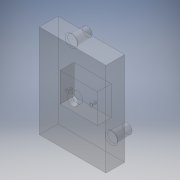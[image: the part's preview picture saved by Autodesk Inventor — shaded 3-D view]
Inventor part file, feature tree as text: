
AUTODESK INVENTOR PART (.ipt)
format: ipt  version: 2019 (Build 230136000, 136)  size: 160,768 bytes
history: native  units: mm
features: reference x14, other x5, extrude x4, sketch x4, fillet x3
ambient origin geometry x8: Origin, YZ Plane, XZ Plane, XY Plane, X Axis, Y Axis, Z Axis, Center Point
bodies: Solid1 (feature_tree)
feature tree (30):
  extrude  "Extrusion1"  Depth=7.0mm TaperAngle=0.0deg
  extrude  "Extrusion3"  Depth=6.0mm
  extrude  "Extrusion4"  Depth=5.2mm
  extrude  "Extrusion5"  Depth=0.2mm
  fillet  "Fillet1"  Radius=0.4mm
  fillet  "Fillet2"  Radius=0.5mm
  fillet  "Fillet3"  Radius=1.0mm
  sketch  "Sketch1"  dims[d0=4.0mm d1=7.0mm d2=0.0mm]
  reference  "Reference1"
  reference  "Reference2"
  reference  "Reference3"
  reference  "Reference4"
  sketch  "Sketch2"  dims[d9=3.8mm d10=6.0mm d11=-0.174533mm]
  reference  "Reference5"
  reference  "Reference6"
  sketch  "Sketch3"  dims[d16=5.2mm d17=0.0mm d18=1.0mm]
  reference  "Reference12"
  reference  "Reference14"
  sketch  "Sketch4"  dims[d19=2.0mm d20=0.0mm d21=0.2mm d22=0.4mm d23=0.5mm d24=1.0mm d25=1.0mm d26=0.5mm d27=0.5mm]
  reference  "Reference15"
  reference  "Reference16"
  reference  "Reference17"
  reference  "Reference18"
  reference  "Reference19"
  reference  "Reference20"
  parser-record x1  (decoder bookkeeping rows leaked as tree rows — omitted from the tree; the rows remain in map.json)
  other  "Kinematics.iam"
  other  "Base:1"
  other  "Motor-GM15BY:1"
  other  "Motor-Body:1"
note: 1 file-system path scrubbed to <path> (originals preserved in map.json)
